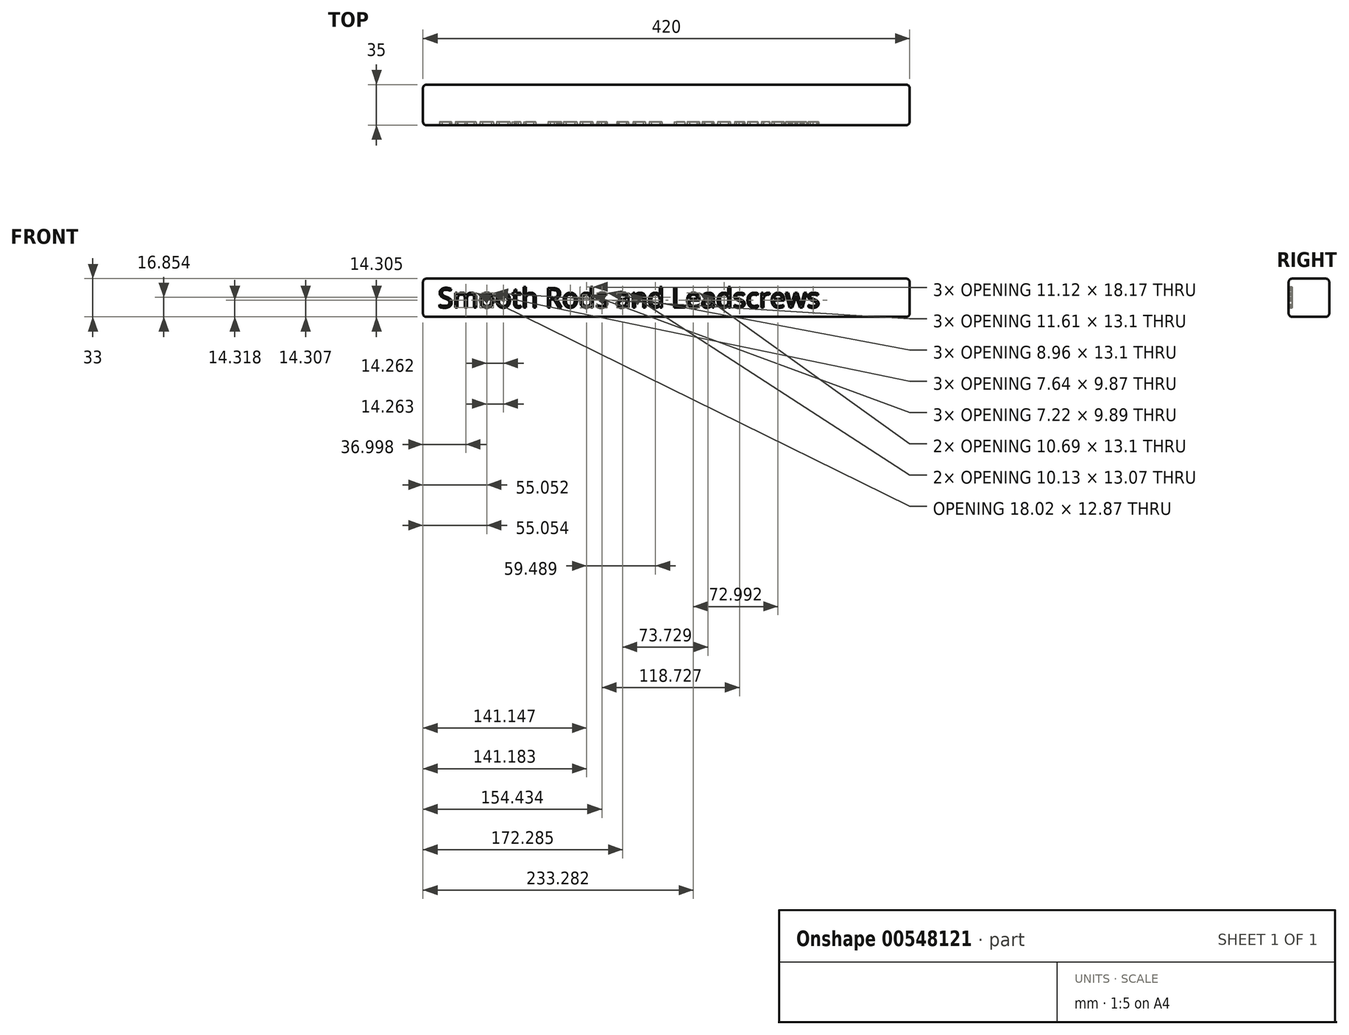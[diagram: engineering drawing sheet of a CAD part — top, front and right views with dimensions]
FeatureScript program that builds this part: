
annotation { "Feature Type Name" : "Feature", "Feature Type Description" : "" }
export const myFeature = defineFeature(function(context is Context, id is Id, definition is map)
    precondition{}
    {
        {
            var Q0;
            Q0=qCreatedBy(makeId("Top.planeOp"),FACE);
            var sketch = newSketch(context, id + "F0", { "sketchPlane" : qUnion([Q0])});
            skLineSegment(sketch, "E0.bottom", {"start": v(0, 0) * mm, "end": v(-420, 0) * mm});
            skLineSegment(sketch, "E0.top", {"start": v(0, 35) * mm, "end": v(-420, 35) * mm});
            skLineSegment(sketch, "E0.left", {"start": v(0, 0) * mm, "end": v(0, 35) * mm});
            skLineSegment(sketch, "E0.right", {"start": v(-420, 0) * mm, "end": v(-420, 35) * mm});
            skSolve(sketch);
        }
        {
            var Q0;
            Q0=makeQuery(id+"F0.imprint","IMPRINT",FACE,{"disambiguationData":[TD([[makeQuery(id+"F0.imprint","IMPRINT",EDGE,{"derivedFrom":sQuery(id+"F0.wireOp",EDGE,"E0.bottom")}),-1.0]])]});
            extrude(context, id + "F1", {"entities" : qUnion([Q0]), "depth" : 33 * mm, "offsetDistance" : 25 * mm});
        }
        {
            var Q0;
            Q0=makeQuery(id+"F1.opExtrude","SWEPT_FACE",FACE,{"disambiguationData":[OSD([sQuery(id+"F0.wireOp",EDGE,"E0.bottom")])]});
            var Q1;
            Q1=makeQuery(id+"F1.opExtrude","CAP_FACE",FACE,{"disambiguationData":[OSD([sQuery(id+"F0.wireOp",EDGE,"E0.bottom"),sQuery(id+"F0.wireOp",EDGE,"E0.top"),sQuery(id+"F0.wireOp",EDGE,"E0.left"),sQuery(id+"F0.wireOp",EDGE,"E0.right")])],"isStart":false});
            var Q2;
            Q2=makeQuery(id+"F1.opExtrude","SWEPT_FACE",FACE,{"disambiguationData":[OSD([sQuery(id+"F0.wireOp",EDGE,"E0.left")])]});
            var Q3;
            Q3=makeQuery(id+"F1.opExtrude","SWEPT_FACE",FACE,{"disambiguationData":[OSD([sQuery(id+"F0.wireOp",EDGE,"E0.top")])]});
            var Q4;
            Q4=makeQuery(id+"F1.opExtrude","CAP_FACE",FACE,{"disambiguationData":[OSD([sQuery(id+"F0.wireOp",EDGE,"E0.bottom"),sQuery(id+"F0.wireOp",EDGE,"E0.top"),sQuery(id+"F0.wireOp",EDGE,"E0.left"),sQuery(id+"F0.wireOp",EDGE,"E0.right")])],"isStart":true});
            fillet(context, id + "F2", {"entities" : qUnion([Q0, Q1, Q2, Q3, Q4]), "radius" : 3 * mm, "tangentPropagation" : true, "allowEdgeOverflow" : false});
        }
        {
            var Q0;
            Q0=makeQuery(id+"F1.opExtrude","SWEPT_FACE",FACE,{"disambiguationData":[OSD([sQuery(id+"F0.wireOp",EDGE,"E0.bottom")])]});
            var sketch = newSketch(context, id + "F3", { "sketchPlane" : qUnion([Q0])});
            skText(sketch, "E1", { "text": "Smooth Rods and Leadscrews", "fontName": "OpenSans-Regular.ttf"});
            const initialGuessF3  = {"E1": [-0.407, 0.008, 1, 0, 0.017]};
            skSetInitialGuess(sketch, initialGuessF3);
            skSolve(sketch);
        }
        {
            var Q0;
            Q0 = qSketchRegion(id + "F3", true);
            extrude(context, id + "F4", {"entities" : qUnion([Q0]), "operationType" : NewBodyOperationType.REMOVE, "oppositeDirection" : true, "depth" : 3 * mm, "offsetDistance" : 25 * mm});
        }
    });
